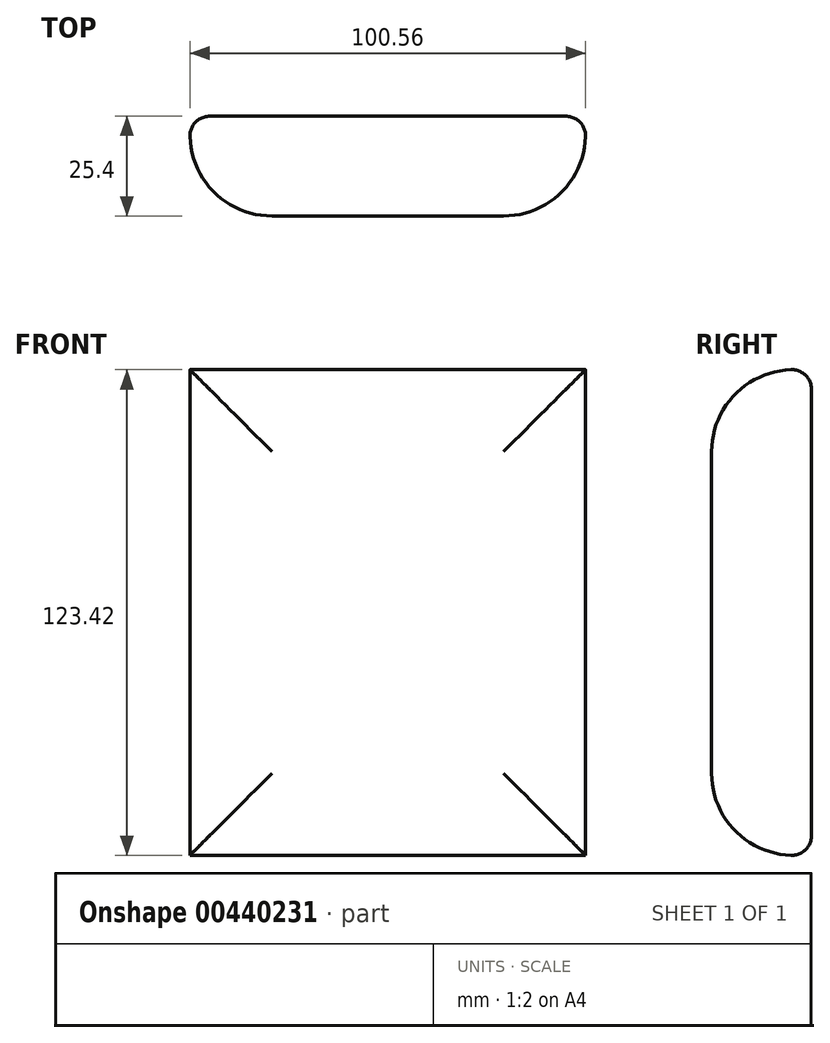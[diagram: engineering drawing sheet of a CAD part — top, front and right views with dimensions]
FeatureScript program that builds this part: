
annotation { "Feature Type Name" : "Feature", "Feature Type Description" : "" }
export const myFeature = defineFeature(function(context is Context, id is Id, definition is map)
    precondition{}
    {
        {
            var Q0;
            Q0=qCreatedBy(makeId("Front.planeOp"),FACE);
            var sketch = newSketch(context, id + "F0", { "sketchPlane" : qUnion([Q0])});
            skLineSegment(sketch, "E0.bottom", {"start": v(-52.73, 61.72) * mm, "end": v(47.85, 61.72) * mm});
            skLineSegment(sketch, "E0.top", {"start": v(-52.73, -61.72) * mm, "end": v(47.85, -61.72) * mm});
            skLineSegment(sketch, "E0.left", {"start": v(-52.73, 61.72) * mm, "end": v(-52.73, -61.72) * mm});
            skLineSegment(sketch, "E0.right", {"start": v(47.85, 61.72) * mm, "end": v(47.85, -61.72) * mm});
            skSolve(sketch);
        }
        {
            var Q0;
            Q0=makeQuery(id+"F0.imprint","IMPRINT",FACE,{"disambiguationData":[TD([[makeQuery(id+"F0.imprint","IMPRINT",EDGE,{"derivedFrom":sQuery(id+"F0.wireOp",EDGE,"E0.bottom")}),-1.0]])]});
            extrude(context, id + "F1", {"entities" : qUnion([Q0]), "depth" : 25.4 * mm});
        }
        {
            var Q0;
            Q0=makeQuery(id+"F1.opExtrude","CAP_EDGE",EDGE,{"disambiguationData":[OSD([sQuery(id+"F0.wireOp",EDGE,"E0.right")])],"isStart":false});
            var Q1;
            Q1=makeQuery(id+"F1.opExtrude","CAP_EDGE",EDGE,{"disambiguationData":[OSD([sQuery(id+"F0.wireOp",EDGE,"E0.bottom")])],"isStart":false});
            var Q2;
            Q2=makeQuery(id+"F1.opExtrude","CAP_FACE",FACE,{"disambiguationData":[OSD([sQuery(id+"F0.wireOp",EDGE,"E0.bottom"),sQuery(id+"F0.wireOp",EDGE,"E0.top"),sQuery(id+"F0.wireOp",EDGE,"E0.left"),sQuery(id+"F0.wireOp",EDGE,"E0.right")])],"isStart":false});
            fillet(context, id + "F2", {"entities" : qUnion([Q0, Q1, Q2]), "radius" : 20.85 * mm, "tangentPropagation" : true, "allowEdgeOverflow" : false});
        }
        {
            var Q0;
            Q0=makeQuery(id+"F1.opExtrude","CAP_EDGE",EDGE,{"disambiguationData":[OSD([sQuery(id+"F0.wireOp",EDGE,"E0.right")])],"isStart":true});
            var Q1;
            Q1=makeQuery(id+"F1.opExtrude","CAP_EDGE",EDGE,{"disambiguationData":[OSD([sQuery(id+"F0.wireOp",EDGE,"E0.bottom")])],"isStart":true});
            var Q2;
            Q2=makeQuery(id+"F1.opExtrude","CAP_EDGE",EDGE,{"disambiguationData":[OSD([sQuery(id+"F0.wireOp",EDGE,"E0.left")])],"isStart":true});
            var Q3;
            Q3=makeQuery(id+"F1.opExtrude","CAP_FACE",FACE,{"disambiguationData":[OSD([sQuery(id+"F0.wireOp",EDGE,"E0.bottom"),sQuery(id+"F0.wireOp",EDGE,"E0.top"),sQuery(id+"F0.wireOp",EDGE,"E0.left"),sQuery(id+"F0.wireOp",EDGE,"E0.right")])],"isStart":true});
            var Q4;
            Q4=makeQuery(id+"F1.opExtrude","CAP_FACE",FACE,{"disambiguationData":[OSD([sQuery(id+"F0.wireOp",EDGE,"E0.bottom"),sQuery(id+"F0.wireOp",EDGE,"E0.top"),sQuery(id+"F0.wireOp",EDGE,"E0.left"),sQuery(id+"F0.wireOp",EDGE,"E0.right")])],"isStart":false});
            fillet(context, id + "F3", {"entities" : qUnion([Q0, Q1, Q2, Q3, Q4]), "radius" : 5.08 * mm, "tangentPropagation" : true, "allowEdgeOverflow" : false});
        }
    });
